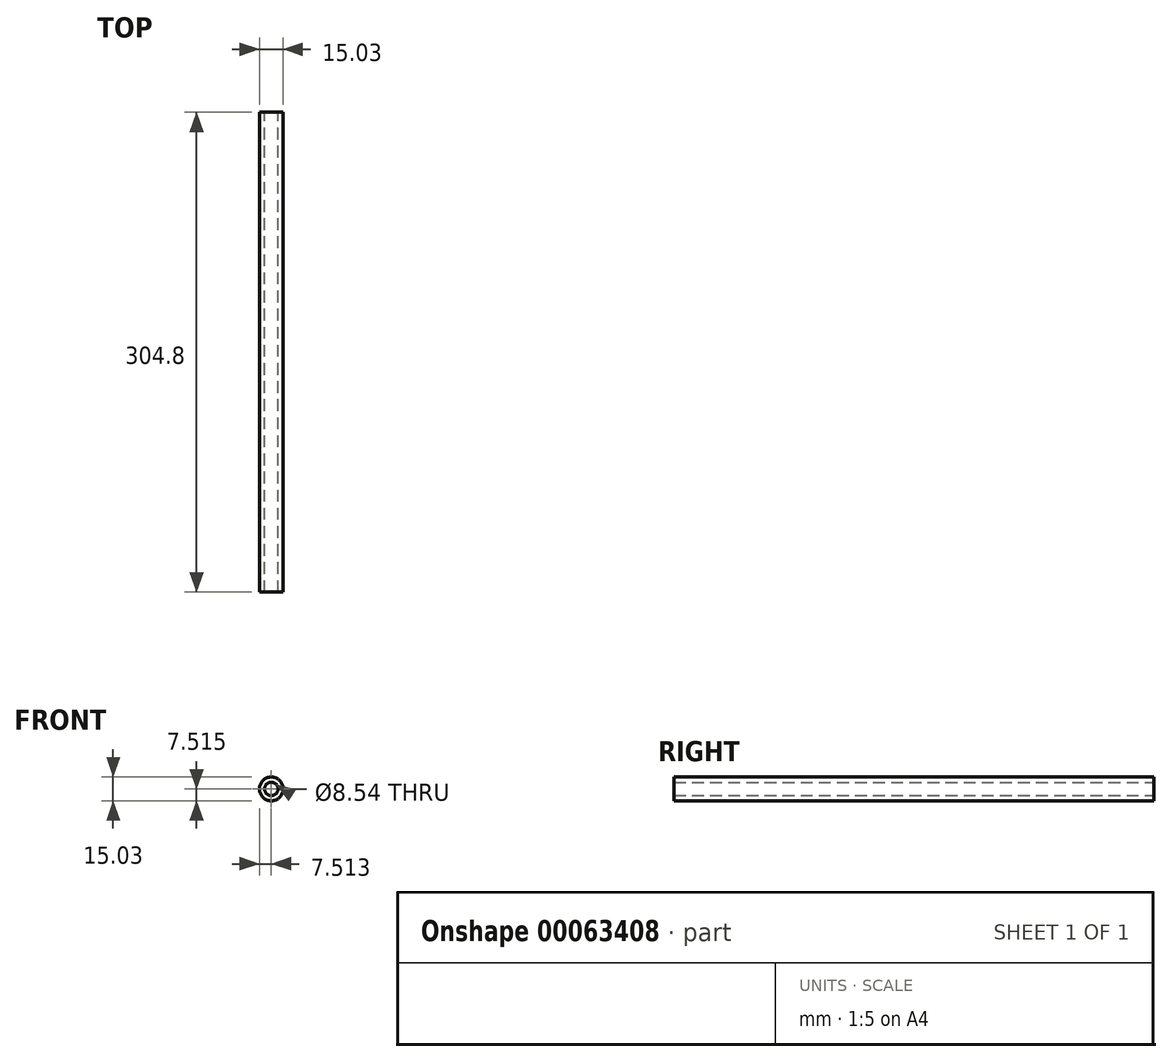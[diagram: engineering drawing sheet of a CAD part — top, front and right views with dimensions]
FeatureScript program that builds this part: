
annotation { "Feature Type Name" : "Feature", "Feature Type Description" : "" }
export const myFeature = defineFeature(function(context is Context, id is Id, definition is map)
    precondition{}
    {
        {
            var Q0;
            Q0=qCreatedBy(makeId("Front.planeOp"),FACE);
            var sketch = newSketch(context, id + "F0", { "sketchPlane" : qUnion([Q0])});
            skCircle(sketch, "E0", {"center": v(0.2, -1.02) * mm, "radius": 4.27 * mm});
            skCircle(sketch, "E1", {"center": v(0.2, -1.02) * mm, "radius": 7.52 * mm});
            skSolve(sketch);
        }
        {
            var Q0;
            Q0=makeQuery(id+"F0.imprint","IMPRINT",FACE,{"disambiguationData":[TD([[makeQuery(id+"F0.imprint","IMPRINT",EDGE,{"derivedFrom":sQuery(id+"F0.wireOp",EDGE,"E0")}),-1.0]])]});
            extrude(context, id + "F1", {"entities" : qUnion([Q0]), "endBound" : BoundingType.SYMMETRIC, "depth" : 304.8 * mm});
        }
    });
